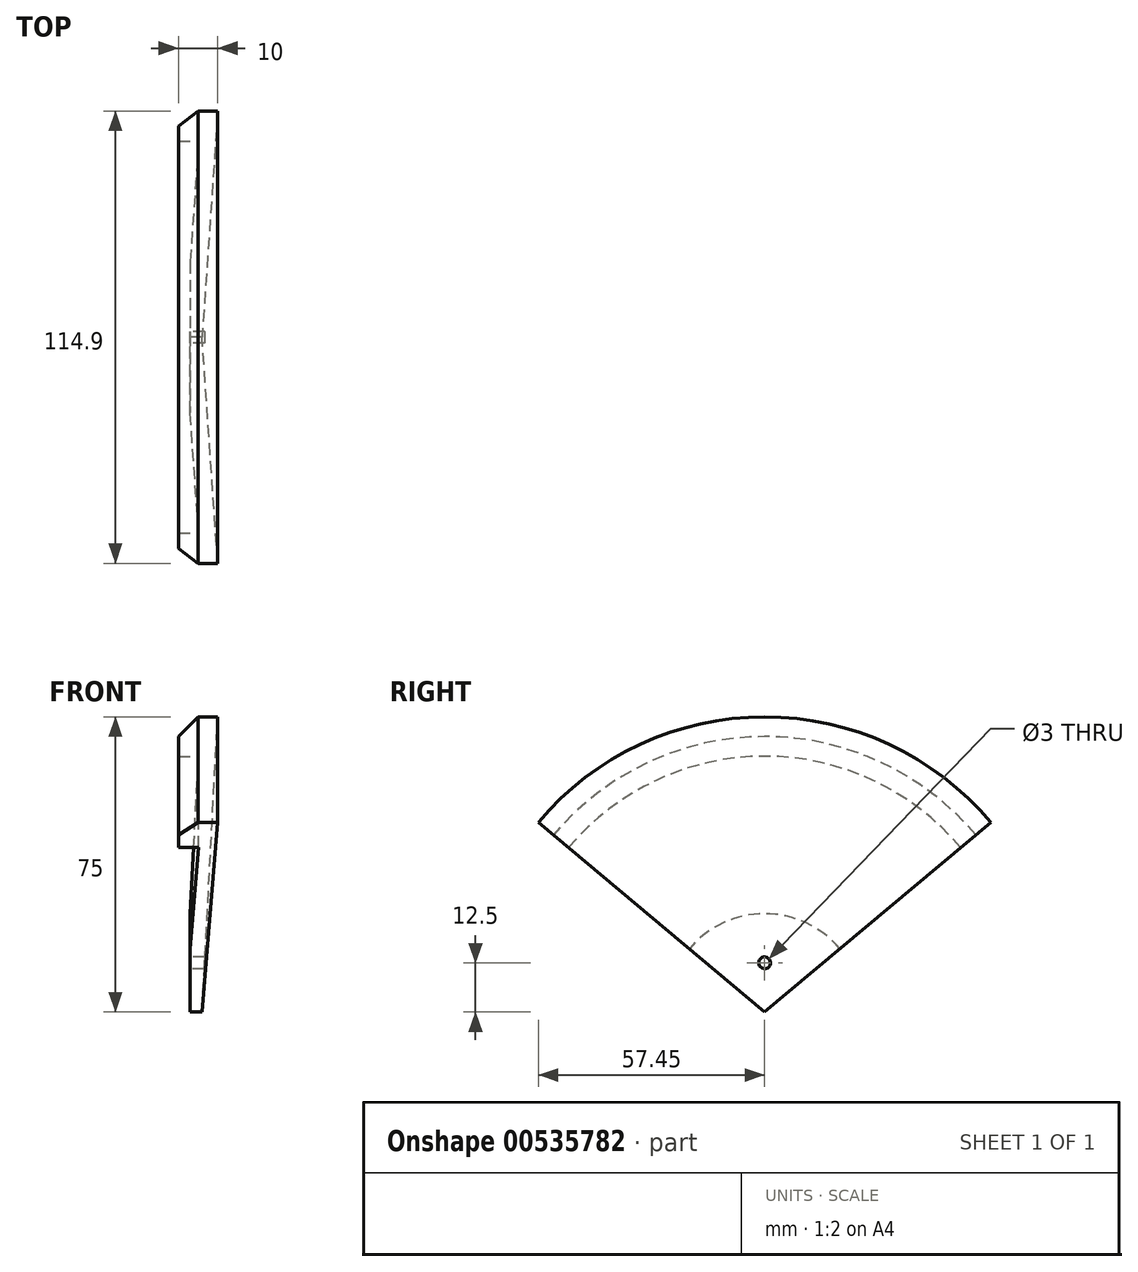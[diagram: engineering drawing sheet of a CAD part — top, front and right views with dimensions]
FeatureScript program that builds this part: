
annotation { "Feature Type Name" : "Feature", "Feature Type Description" : "" }
export const myFeature = defineFeature(function(context is Context, id is Id, definition is map)
    precondition{}
    {
        {
            var Q0;
            Q0=qCreatedBy(makeId("Front.planeOp"),FACE);
            var sketch = newSketch(context, id + "F0", { "sketchPlane" : qUnion([Q0])});
            skLineSegment(sketch, "E0", {"start": v(7, 75) * mm, "end": v(-3, 75) * mm});
            skLineSegment(sketch, "E1", {"start": v(-3, 75) * mm, "end": v(-3, 65) * mm});
            skLineSegment(sketch, "E2", {"start": v(-3, 65) * mm, "end": v(2.13, 65) * mm});
            skLineSegment(sketch, "E3", {"start": v(2.13, 65) * mm, "end": v(0, 25) * mm});
            skLineSegment(sketch, "E4", {"start": v(0, 25) * mm, "end": v(0, 0) * mm});
            skLineSegment(sketch, "E5", {"start": v(-52.2, 0) * mm, "end": v(67.72, 0) * mm, "construction": true});
            skLineSegment(sketch, "E6", {"start": v(7, 75) * mm, "end": v(3, 0) * mm});
            skLineSegment(sketch, "E7", {"start": v(3, 0) * mm, "end": v(0, 0) * mm});
            skSolve(sketch);
        }
        {
            var Q0;
            Q0=makeQuery(id+"F0.imprint","IMPRINT",FACE,{"disambiguationData":[TD([[makeQuery(id+"F0.imprint","IMPRINT",EDGE,{"derivedFrom":sQuery(id+"F0.wireOp",EDGE,"E0")}),1.0]])]});
            var Q1;
            Q1=sQuery(id+"F0.wireOp",EDGE,"E7");
            revolve(context, id + "F1", {"entities" : qUnion([Q0]), "axis" : qUnion([Q1]), "revolveType" : RevolveType.SYMMETRIC, "angle" : 100 * degree});
        }
        {
            var Q0;
            Q0=makeQuery(id+"F1.opRevolve","SWEPT_EDGE",EDGE,{"disambiguationData":[OSD([sQuery(id+"F0.wireOp",EDGE,"E0"),sQuery(id+"F0.wireOp",EDGE,"E1")])]});
            chamfer(context, id + "F2", {"entities" : qUnion([Q0]), "width" : 5 * mm, "tangentPropagation" : true});
        }
        {
            var Q0;
            Q0=qCreatedBy(makeId("Right.planeOp"),FACE);
            var sketch = newSketch(context, id + "F3", { "sketchPlane" : qUnion([Q0])});
            skCircle(sketch, "E8", {"center": v(0, 12.5) * mm, "radius": 1.5 * mm});
            skArc(sketch, "E9.0", {"start": v(19.15, 16.07) * mm, "mid": v(0, 25) * mm, "end": v(-19.15, 16.07) * mm});
            skLineSegment(sketch, "E10.0.0", {"start": v(19.15, 16.07) * mm, "end": v(0, 0) * mm, "construction": true});
            skLineSegment(sketch, "E10.0.1", {"start": v(0, 0) * mm, "end": v(-19.15, 16.07) * mm, "construction": true});
            skArc(sketch, "E10.0.2", {"start": v(-19.15, 16.07) * mm, "mid": v(0, 25) * mm, "end": v(19.15, 16.07) * mm, "construction": true});
            skLineSegment(sketch, "E11", {"start": v(0, 25) * mm, "end": v(0, 0) * mm, "construction": true});
            skSolve(sketch);
        }
        {
            var Q0;
            Q0=makeQuery(id+"F3.imprint","IMPRINT",FACE,{"disambiguationData":[TD([[makeQuery(id+"F3.imprint","IMPRINT",EDGE,{"derivedFrom":sQuery(id+"F3.wireOp",EDGE,"E8")}),1.0]])]});
            var Q1;
            Q1=sQuery(id+"F3.wireOp",EDGE,"E8");
            extrude(context, id + "F4", {"entities" : qUnion([Q0]), "operationType" : NewBodyOperationType.REMOVE, "surfaceEntities" : qUnion([Q1]), "endBound" : BoundingType.UP_TO_NEXT, "depth" : 25 * mm, "offsetDistance" : 25 * mm});
        }
    });
